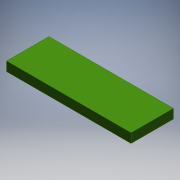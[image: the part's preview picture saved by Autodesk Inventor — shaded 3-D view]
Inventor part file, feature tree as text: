
AUTODESK INVENTOR PART (.ipt)
format: ipt  version: 2016 (Build 200138000, 138)  size: 96,256 bytes
history: native  units: mm
features: extrude x1, sketch x1
ambient origin geometry x8: Origin, YZ Plane, XZ Plane, XY Plane, X Axis, Y Axis, Z Axis, Center Point
bodies: Solid1 (feature_tree)
feature tree (2):
  extrude  "Extrusion1"  Depth=40.0mm
  sketch  "Sketch1"  dims[d0=13.6mm d1=40.0mm d2=20.0mm d3=6.8mm d4=3.0mm d5=0.0mm]
